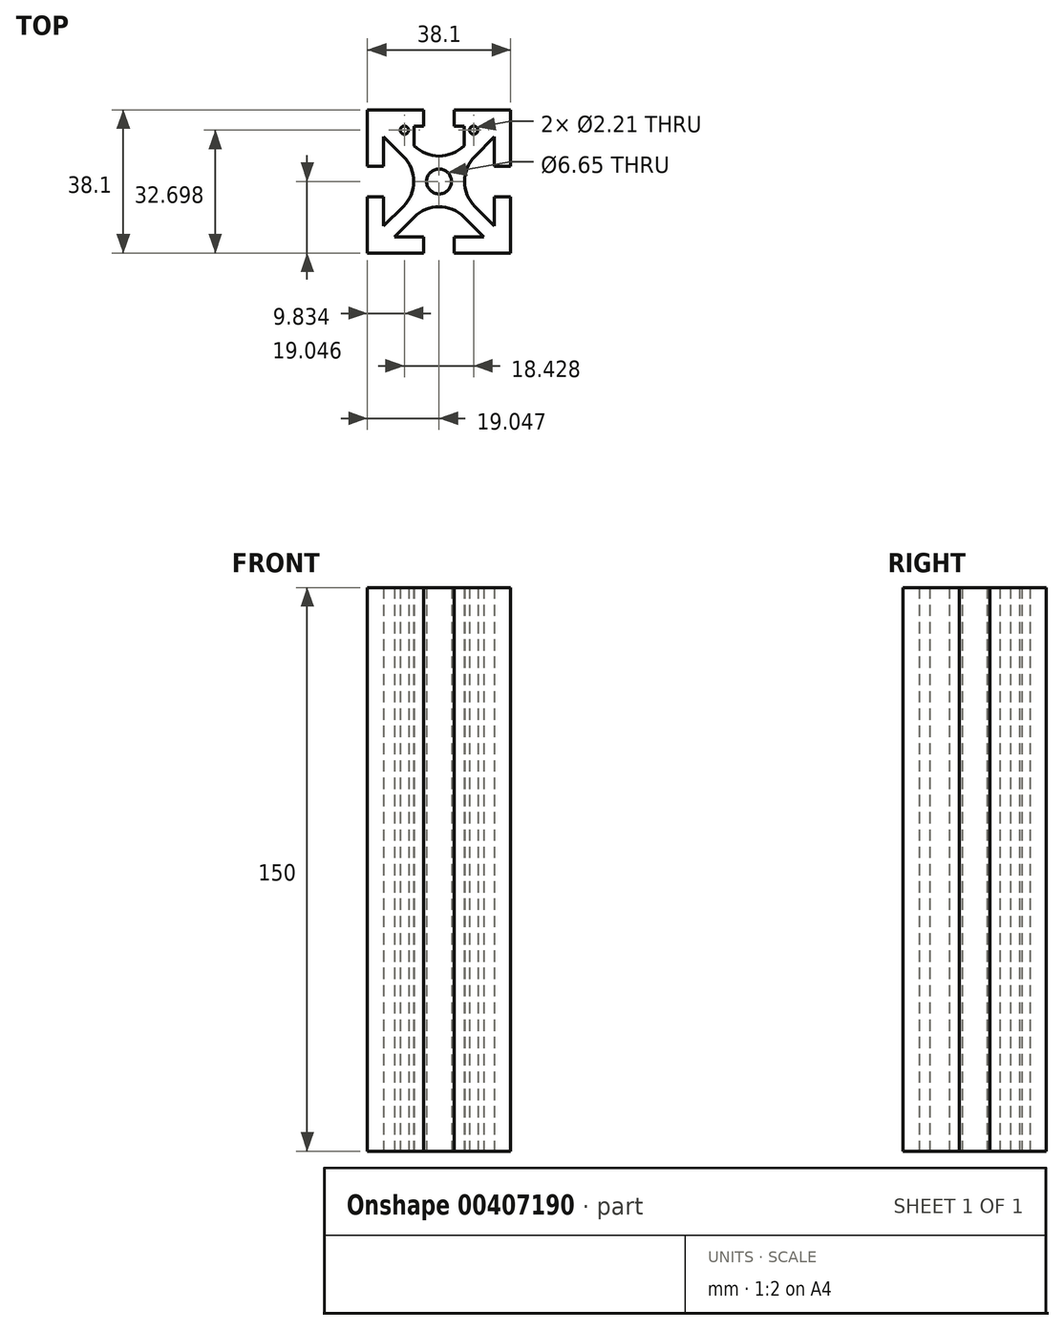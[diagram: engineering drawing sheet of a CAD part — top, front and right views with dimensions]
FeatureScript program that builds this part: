
annotation { "Feature Type Name" : "Feature", "Feature Type Description" : "" }
export const myFeature = defineFeature(function(context is Context, id is Id, definition is map)
    precondition{}
    {
        {
            var Q0;
            Q0=qCreatedBy(makeId("Top.planeOp"),FACE);
            var sketch = newSketch(context, id + "F0", { "sketchPlane" : qUnion([Q0])});
            skLineSegment(sketch, "E0.1.1", {"start": v(4.4, -19.7) * mm, "end": v(4.4, -15.41) * mm});
            skArc(sketch, "E1", {"start": v(-9.17, -7.28) * mm, "mid": v(-6.43, -0.65) * mm, "end": v(-9.17, 5.97) * mm});
            skLineSegment(sketch, "E2", {"start": v(-6.43, 3.23) * mm, "end": v(4.21, -7.41) * mm, "construction": true});
            skLineSegment(sketch, "E3", {"start": v(-3.74, -19.7) * mm, "end": v(-18.72, -19.7) * mm});
            skLineSegment(sketch, "E4", {"start": v(-11.56, 14.1) * mm, "end": v(-6.3, 8.85) * mm});
            skLineSegment(sketch, "E5", {"start": v(-6.3, 8.85) * mm, "end": v(-6.3, 14.1) * mm});
            skLineSegment(sketch, "E6", {"start": v(-3.74, 14.1) * mm, "end": v(4.4, 14.1) * mm, "construction": true});
            skLineSegment(sketch, "E0.2.0", {"start": v(19.38, -4.72) * mm, "end": v(15.08, -4.72) * mm});
            skLineSegment(sketch, "E7", {"start": v(-9.17, 5.97) * mm, "end": v(-6.43, 3.23) * mm, "construction": true});
            skLineSegment(sketch, "E8", {"start": v(-3.56, 6.1) * mm, "end": v(7.08, -4.54) * mm, "construction": true});
            skLineSegment(sketch, "E9", {"start": v(15.08, 14.1) * mm, "end": v(15.08, 3.41) * mm});
            skLineSegment(sketch, "E10", {"start": v(-14.43, 11.23) * mm, "end": v(-9.17, 5.97) * mm});
            skLineSegment(sketch, "E11", {"start": v(6.96, 8.85) * mm, "end": v(6.96, 14.1) * mm});
            skLineSegment(sketch, "E12", {"start": v(4.4, -15.41) * mm, "end": v(15.08, -15.41) * mm});
            skLineSegment(sketch, "E13", {"start": v(4.4, 14.1) * mm, "end": v(15.08, 14.1) * mm});
            skLineSegment(sketch, "E0.3.0", {"start": v(4.4, 18.4) * mm, "end": v(4.4, 14.1) * mm});
            skLineSegment(sketch, "E14.0", {"start": v(-18.72, -4.72) * mm, "end": v(-14.43, -4.72) * mm});
            skLineSegment(sketch, "E15", {"start": v(-6.3, -10.16) * mm, "end": v(-11.56, -15.41) * mm});
            skLineSegment(sketch, "E16", {"start": v(7.08, 3.23) * mm, "end": v(-3.56, -7.41) * mm, "construction": true});
            skLineSegment(sketch, "E17", {"start": v(-9.17, -7.28) * mm, "end": v(-14.43, -12.54) * mm});
            skLineSegment(sketch, "E18", {"start": v(4.21, 6.1) * mm, "end": v(-6.43, -4.54) * mm, "construction": true});
            skLineSegment(sketch, "E19", {"start": v(15.08, -4.72) * mm, "end": v(15.08, -15.41) * mm});
            skLineSegment(sketch, "E20", {"start": v(12.21, -15.41) * mm, "end": v(16.5, -19.7) * mm, "construction": true});
            skLineSegment(sketch, "E21", {"start": v(-3.74, -15.41) * mm, "end": v(-14.43, -15.41) * mm});
            skLineSegment(sketch, "E22", {"start": v(-18.72, 18.4) * mm, "end": v(-3.74, 18.4) * mm});
            skLineSegment(sketch, "E0.3.1", {"start": v(-3.74, 18.4) * mm, "end": v(-3.74, 14.1) * mm});
            skLineSegment(sketch, "E23.0.MirrorCS", {"start": v(-18.72, 3.41) * mm, "end": v(-14.43, 3.41) * mm});
            skLineSegment(sketch, "E24", {"start": v(9.83, -7.28) * mm, "end": v(15.08, -12.54) * mm});
            skLineSegment(sketch, "E25", {"start": v(7.08, -4.54) * mm, "end": v(9.83, -7.28) * mm, "construction": true});
            skPoint(sketch, "E26", {"position": v(0.33, -0.65) * mm});
            skLineSegment(sketch, "E27", {"start": v(15.08, -12.54) * mm, "end": v(19.38, -16.83) * mm, "construction": true});
            skCircle(sketch, "E28", {"center": v(-8.89, 13) * mm, "radius": 1.1 * mm});
            skLineSegment(sketch, "E29", {"start": v(4.4, 18.4) * mm, "end": v(19.38, 18.4) * mm});
            skLineSegment(sketch, "E30", {"start": v(-14.43, 3.41) * mm, "end": v(-14.43, -4.72) * mm, "construction": true});
            skLineSegment(sketch, "E31", {"start": v(0.33, -0.65) * mm, "end": v(0.33, 18.4) * mm, "construction": true});
            skLineSegment(sketch, "E32", {"start": v(9.83, 5.97) * mm, "end": v(7.08, 3.23) * mm, "construction": true});
            skArc(sketch, "E33", {"start": v(-6.3, 8.85) * mm, "mid": v(0.33, 6.1) * mm, "end": v(6.96, 8.85) * mm});
            skLineSegment(sketch, "E34", {"start": v(4.21, -7.41) * mm, "end": v(6.96, -10.16) * mm, "construction": true});
            skLineSegment(sketch, "E35.top", {"start": v(-14.43, -15.41) * mm, "end": v(15.08, -15.41) * mm, "construction": true});
            skLineSegment(sketch, "E35.left", {"start": v(-14.43, 14.1) * mm, "end": v(-14.43, 3.41) * mm});
            skLineSegment(sketch, "E35.right", {"start": v(15.08, 14.1) * mm, "end": v(15.08, -15.41) * mm, "construction": true});
            skCircle(sketch, "E36", {"center": v(0.33, -0.65) * mm, "radius": 3.33 * mm});
            skLineSegment(sketch, "E37.bottom", {"start": v(-6.43, 6.1) * mm, "end": v(7.08, 6.1) * mm, "construction": true});
            skLineSegment(sketch, "E37.top", {"start": v(-6.43, -7.41) * mm, "end": v(7.08, -7.41) * mm, "construction": true});
            skLineSegment(sketch, "E37.left", {"start": v(-6.43, 6.1) * mm, "end": v(-6.43, -7.41) * mm, "construction": true});
            skLineSegment(sketch, "E37.right", {"start": v(7.08, 6.1) * mm, "end": v(7.08, -7.41) * mm, "construction": true});
            skLineSegment(sketch, "E38.bottom", {"start": v(-18.72, 18.4) * mm, "end": v(19.38, 18.4) * mm, "construction": true});
            skLineSegment(sketch, "E38.top", {"start": v(-18.72, -19.7) * mm, "end": v(19.38, -19.7) * mm, "construction": true});
            skLineSegment(sketch, "E38.left", {"start": v(-18.72, 18.4) * mm, "end": v(-18.72, 3.41) * mm});
            skLineSegment(sketch, "E38.right", {"start": v(19.38, 18.4) * mm, "end": v(19.38, -19.7) * mm, "construction": true});
            skLineSegment(sketch, "E39", {"start": v(-18.72, 18.4) * mm, "end": v(19.38, -19.7) * mm, "construction": true});
            skLineSegment(sketch, "E35.bottom", {"start": v(-14.43, 14.1) * mm, "end": v(-3.74, 14.1) * mm});
            skLineSegment(sketch, "E40", {"start": v(0.33, -0.65) * mm, "end": v(19.38, -0.65) * mm, "construction": true});
            skLineSegment(sketch, "E41", {"start": v(-6.3, 8.85) * mm, "end": v(-3.56, 6.1) * mm, "construction": true});
            skLineSegment(sketch, "E42", {"start": v(7.08, 6.1) * mm, "end": v(-6.43, -7.41) * mm, "construction": true});
            skLineSegment(sketch, "E43", {"start": v(19.38, 18.4) * mm, "end": v(19.38, 3.41) * mm});
            skLineSegment(sketch, "E44", {"start": v(-18.72, 18.4) * mm, "end": v(-6.43, 6.1) * mm, "construction": true});
            skCircle(sketch, "E45", {"center": v(9.54, 13) * mm, "radius": 1.1 * mm});
            skLineSegment(sketch, "E46", {"start": v(-14.43, -4.72) * mm, "end": v(-14.43, -15.41) * mm});
            skArc(sketch, "E47", {"start": v(6.96, -10.16) * mm, "mid": v(0.33, -7.41) * mm, "end": v(-6.3, -10.16) * mm});
            skLineSegment(sketch, "E48", {"start": v(-3.56, -7.41) * mm, "end": v(-6.3, -10.16) * mm, "construction": true});
            skLineSegment(sketch, "E49", {"start": v(0.33, -0.65) * mm, "end": v(0.33, -19.7) * mm, "construction": true});
            skLineSegment(sketch, "E50.0", {"start": v(12.21, 14.1) * mm, "end": v(6.96, 8.85) * mm});
            skLineSegment(sketch, "E51", {"start": v(19.38, -4.72) * mm, "end": v(19.38, -19.7) * mm});
            skLineSegment(sketch, "E52.0", {"start": v(-18.72, 15.52) * mm, "end": v(-14.43, 11.23) * mm, "construction": true});
            skLineSegment(sketch, "E53", {"start": v(-18.72, -4.72) * mm, "end": v(-18.72, -19.7) * mm});
            skLineSegment(sketch, "E54", {"start": v(6.96, -10.16) * mm, "end": v(12.21, -15.41) * mm});
            skLineSegment(sketch, "E55", {"start": v(-6.43, -4.54) * mm, "end": v(-9.17, -7.28) * mm, "construction": true});
            skLineSegment(sketch, "E56", {"start": v(6.96, -10.16) * mm, "end": v(6.96, -10.16) * mm});
            skLineSegment(sketch, "E0.1.0", {"start": v(-3.74, -19.7) * mm, "end": v(-3.74, -15.41) * mm});
            skArc(sketch, "E57", {"start": v(9.83, 5.97) * mm, "mid": v(7.08, -0.65) * mm, "end": v(9.83, -7.28) * mm});
            skLineSegment(sketch, "E58.0.MirrorCS", {"start": v(15.08, 11.23) * mm, "end": v(9.83, 5.97) * mm});
            skLineSegment(sketch, "E59", {"start": v(4.4, -19.7) * mm, "end": v(19.38, -19.7) * mm});
            skLineSegment(sketch, "E60.0.MirrorCS", {"start": v(-15.85, 18.4) * mm, "end": v(-11.56, 14.1) * mm, "construction": true});
            skLineSegment(sketch, "E61", {"start": v(-18.72, 3.41) * mm, "end": v(-18.72, -4.72) * mm, "construction": true});
            skLineSegment(sketch, "E62", {"start": v(0.33, -0.65) * mm, "end": v(-18.72, -0.65) * mm, "construction": true});
            skLineSegment(sketch, "E63", {"start": v(-6.43, 3.23) * mm, "end": v(-6.43, -4.54) * mm, "construction": true});
            skLineSegment(sketch, "E64", {"start": v(-18.72, -0.65) * mm, "end": v(-14.43, -0.65) * mm, "construction": true});
            skLineSegment(sketch, "E65", {"start": v(-3.56, -7.41) * mm, "end": v(4.21, -7.41) * mm, "construction": true});
            skLineSegment(sketch, "E66", {"start": v(7.08, -4.54) * mm, "end": v(7.08, 3.23) * mm, "construction": true});
            skLineSegment(sketch, "E0.2.1", {"start": v(19.38, 3.41) * mm, "end": v(15.08, 3.41) * mm});
            skLineSegment(sketch, "E67", {"start": v(4.21, 6.1) * mm, "end": v(-3.56, 6.1) * mm, "construction": true});
            skLineSegment(sketch, "E68", {"start": v(-6.43, 6.1) * mm, "end": v(7.08, -7.41) * mm, "construction": true});
            skLineSegment(sketch, "E69", {"start": v(6.96, 8.85) * mm, "end": v(4.21, 6.1) * mm, "construction": true});
            skLineSegment(sketch, "E70", {"start": v(-8.89, 13) * mm, "end": v(-10, 13) * mm, "construction": true});
            skLineSegment(sketch, "E71", {"start": v(9.54, 13) * mm, "end": v(10.65, 13) * mm, "construction": true});
            skSolve(sketch);
        }
        {
            var Q0;
            Q0=makeQuery(id+"F0.imprint","IMPRINT",FACE,{"disambiguationData":[TD([[makeQuery(id+"F0.imprint","IMPRINT",EDGE,{"derivedFrom":sQuery(id+"F0.wireOp",EDGE,"E3")}),-1.0]])]});
            var Q1;
            Q1=makeQuery(id+"F0.imprint","IMPRINT",FACE,{"disambiguationData":[TD([[makeQuery(id+"F0.imprint","IMPRINT",EDGE,{"derivedFrom":sQuery(id+"F0.wireOp",EDGE,"E1")}),-1.0]])]});
            var Q2;
            {var subQ4=sQuery(id+"F0.wireOp",EDGE,"E0.1.1");Q2=makeQuery(id+"F0.imprint","IMPRINT",FACE,{"disambiguationData":[TD([[makeQuery(id+"F0.imprint","IMPRINT",EDGE,{"derivedFrom":subQ4}),-1.0]])]});}
            var Q3;
            {var subQ7=sQuery(id+"F0.wireOp",EDGE,"E0.3.0");Q3=makeQuery(id+"F0.imprint","IMPRINT",FACE,{"disambiguationData":[TD([[makeQuery(id+"F0.imprint","IMPRINT",EDGE,{"derivedFrom":subQ7}),1.0]])]});}
            var Q4;
            Q4=makeQuery(id+"F0.imprint","IMPRINT",FACE,{"disambiguationData":[TD([[makeQuery(id+"F0.imprint","IMPRINT",EDGE,{"derivedFrom":sQuery(id+"F0.wireOp",EDGE,"E22")}),-1.0]])]});
            var Q5;
            {var subQ0=sQuery(id+"F0.wireOp",EDGE,"E11");Q5=makeQuery(id+"F0.imprint","IMPRINT",FACE,{"disambiguationData":[TD([[makeQuery(id+"F0.imprint","IMPRINT",EDGE,{"derivedFrom":subQ0}),-1.0]])]});}
            var Q6;
            {var subQ0=sQuery(id+"F0.wireOp",EDGE,"E5");Q6=makeQuery(id+"F0.imprint","IMPRINT",FACE,{"disambiguationData":[TD([[makeQuery(id+"F0.imprint","IMPRINT",EDGE,{"derivedFrom":subQ0}),1.0]])]});}
            var Q7;
            {var subQ0=sQuery(id+"F0.wireOp",EDGE,"E50.0");var subQ1=sQuery(id+"F0.wireOp",EDGE,"E13");var subQ2=makeQuery(id+"F0.imprint","INTERSECT",VERTEX,{"derivedFrom":[subQ1,subQ0]});Q7=makeQuery(id+"F0.imprint","IMPRINT",FACE,{"disambiguationData":[TD([[makeQuery(id+"F0.imprint","IMPRINT",EDGE,{"disambiguationData":[TD([[subQ2,1.0]])],"derivedFrom":subQ1}),-1.0]])]});}
            var Q8;
            {var subQ0=sQuery(id+"F0.wireOp",EDGE,"E35.bottom");var subQ1=sQuery(id+"F0.wireOp",EDGE,"E4");var subQ2=makeQuery(id+"F0.imprint","INTERSECT",VERTEX,{"derivedFrom":[subQ1,subQ0]});Q8=makeQuery(id+"F0.imprint","IMPRINT",FACE,{"disambiguationData":[TD([[makeQuery(id+"F0.imprint","IMPRINT",EDGE,{"disambiguationData":[TD([[subQ2,-1.0]])],"derivedFrom":subQ1}),1.0]])]});}
            extrude(context, id + "F1", {"entities" : qUnion([Q0, Q1, Q2, Q3, Q4, Q5, Q6, Q7, Q8]), "depth" : 150 * mm});
        }
    });
